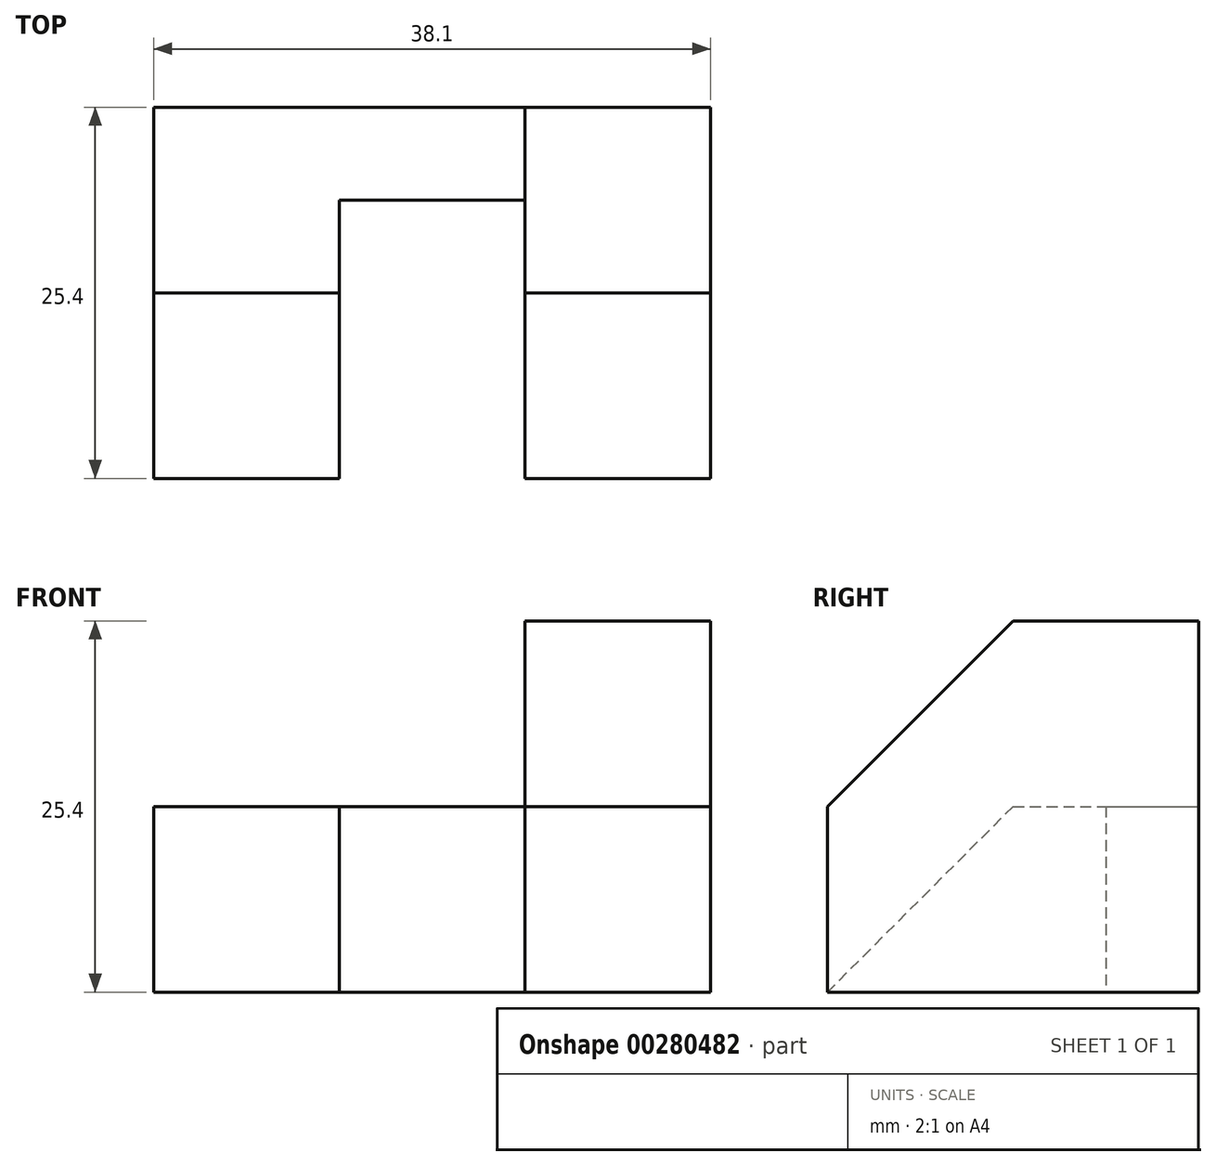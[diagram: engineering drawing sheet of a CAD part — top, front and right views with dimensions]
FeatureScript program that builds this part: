
annotation { "Feature Type Name" : "Feature", "Feature Type Description" : "" }
export const myFeature = defineFeature(function(context is Context, id is Id, definition is map)
    precondition{}
    {
        {
            var Q0;
            Q0=qCreatedBy(makeId("Front.planeOp"),FACE);
            var sketch = newSketch(context, id + "F0", { "sketchPlane" : qUnion([Q0])});
            skLineSegment(sketch, "E0.bottom", {"start": v(0, 0) * mm, "end": v(38.1, 0) * mm});
            skLineSegment(sketch, "E0.top", {"start": v(0, 25.4) * mm, "end": v(38.1, 25.4) * mm});
            skLineSegment(sketch, "E0.left", {"start": v(0, 0) * mm, "end": v(0, 25.4) * mm});
            skLineSegment(sketch, "E0.right", {"start": v(38.1, 0) * mm, "end": v(38.1, 25.4) * mm});
            skSolve(sketch);
        }
        {
            var Q0;
            Q0=makeQuery(id+"F0.imprint","IMPRINT",FACE,{"disambiguationData":[TD([[makeQuery(id+"F0.imprint","IMPRINT",EDGE,{"derivedFrom":sQuery(id+"F0.wireOp",EDGE,"E0.bottom")}),1.0]])]});
            extrude(context, id + "F1", {"entities" : qUnion([Q0]), "endBound" : BoundingType.SYMMETRIC, "oppositeDirection" : true, "depth" : 25.4 * mm});
        }
        {
            var Q0;
            Q0=qCreatedBy(makeId("Right.planeOp"),FACE);
            var sketch = newSketch(context, id + "F2", { "sketchPlane" : qUnion([Q0])});
            skLineSegment(sketch, "E1", {"start": v(0, 25.4) * mm, "end": v(-12.7, 25.4) * mm});
            skLineSegment(sketch, "E2", {"start": v(-12.7, 25.4) * mm, "end": v(-12.7, 0) * mm});
            skLineSegment(sketch, "E3", {"start": v(-12.7, 0) * mm, "end": v(0, 12.7) * mm});
            skLineSegment(sketch, "E4", {"start": v(0, 12.7) * mm, "end": v(0, 25.4) * mm});
            skSolve(sketch);
        }
        {
            var Q0;
            Q0 = qSketchRegion(id + "F2", true);
            extrude(context, id + "F3", {"entities" : qUnion([Q0]), "operationType" : NewBodyOperationType.REMOVE, "depth" : 25.4 * mm});
        }
        {
            var Q0;
            Q0=qCreatedBy(makeId("Top.planeOp"),FACE);
            var sketch = newSketch(context, id + "F4", { "sketchPlane" : qUnion([Q0])});
            skLineSegment(sketch, "E5", {"start": v(12.7, -12.7) * mm, "end": v(12.7, 6.35) * mm});
            skLineSegment(sketch, "E6", {"start": v(12.7, 6.35) * mm, "end": v(25.4, 6.35) * mm});
            skLineSegment(sketch, "E7", {"start": v(25.4, 6.35) * mm, "end": v(25.4, -12.7) * mm});
            skLineSegment(sketch, "E8", {"start": v(25.4, -12.7) * mm, "end": v(12.7, -12.7) * mm});
            skSolve(sketch);
        }
        {
            var Q0;
            Q0 = qSketchRegion(id + "F4", true);
            extrude(context, id + "F5", {"entities" : qUnion([Q0]), "operationType" : NewBodyOperationType.REMOVE, "depth" : 46.48 * mm});
        }
        {
            var Q0;
            Q0=qCreatedBy(makeId("Right.planeOp"),FACE);
            var sketch = newSketch(context, id + "F6", { "sketchPlane" : qUnion([Q0])});
            skLineSegment(sketch, "E9", {"start": v(0, 25.4) * mm, "end": v(-12.7, 25.4) * mm});
            skLineSegment(sketch, "E10", {"start": v(-12.7, 25.4) * mm, "end": v(-12.7, 12.7) * mm});
            skLineSegment(sketch, "E11", {"start": v(-12.7, 12.7) * mm, "end": v(0, 25.4) * mm});
            skSolve(sketch);
        }
        {
            var Q0;
            Q0 = qSketchRegion(id + "F6", true);
            extrude(context, id + "F7", {"entities" : qUnion([Q0]), "operationType" : NewBodyOperationType.REMOVE, "depth" : 79 * mm});
        }
        {
            var Q0;
            Q0=qCreatedBy(makeId("Right.planeOp"),FACE);
            var sketch = newSketch(context, id + "F8", { "sketchPlane" : qUnion([Q0])});
            skLineSegment(sketch, "E12", {"start": v(0, 25.4) * mm, "end": v(0, 12.7) * mm});
            skLineSegment(sketch, "E13", {"start": v(0, 12.7) * mm, "end": v(12.7, 12.7) * mm});
            skLineSegment(sketch, "E14", {"start": v(12.7, 12.7) * mm, "end": v(12.7, 25.4) * mm});
            skLineSegment(sketch, "E15", {"start": v(12.7, 25.4) * mm, "end": v(0, 25.4) * mm});
            skSolve(sketch);
        }
        {
            var Q0;
            Q0 = qSketchRegion(id + "F8", true);
            extrude(context, id + "F9", {"entities" : qUnion([Q0]), "operationType" : NewBodyOperationType.REMOVE, "depth" : 25.4 * mm});
        }
    });
